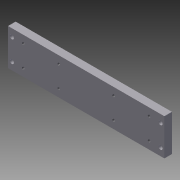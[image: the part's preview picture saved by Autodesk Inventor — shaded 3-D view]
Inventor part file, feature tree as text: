
AUTODESK INVENTOR PART (.ipt)
format: ipt  version: 2012 (Build 160160000, 160)  size: 102,912 bytes
history: native  units: in
note: dims shown in document units (in); Inventor stores cm internally (conversion verified against a paired STEP export)
features: reference x8, sketch x3, hole x2, extrude x1
ambient origin geometry x8: Origin, YZ Plane, XZ Plane, XY Plane, X Axis, Y Axis, Z Axis, Center Point
bodies: Solid1 (feature_tree)
feature tree (14):
  extrude  "Extrusion1"  Depth=7.7in
  hole  "Hole1"  [1 undecoded]
  hole  "Hole2"  [1 undecoded]
  sketch  "Sketch1"  dims[d0=1.8in d1=7.7in]
  sketch  "Sketch2"  dims[d2=0.375in d3=0.0in]
  reference  "Reference1"
  reference  "Reference2"
  reference  "Reference3"
  reference  "Reference4"
  reference  "Reference5"
  reference  "Reference6"
  reference  "Reference7"
  reference  "Reference8"
  sketch  "Sketch3"  dims[d4=0.13in d5=1.0in d6=0.375in d7=0.25in d8=0.5635in d9=1.0in d10=0.8108in d11=0.177in d12=1.0in d13=0.332in d14=0.25in d15=0.5635in d16=1.0in d17=0.8108in d18=0.375in]
note: 2 required parameter values undecoded (feature->parameter linkage not recoverable at this tier; creation-order binding heuristic only, values carry confidence <= 0.55)
